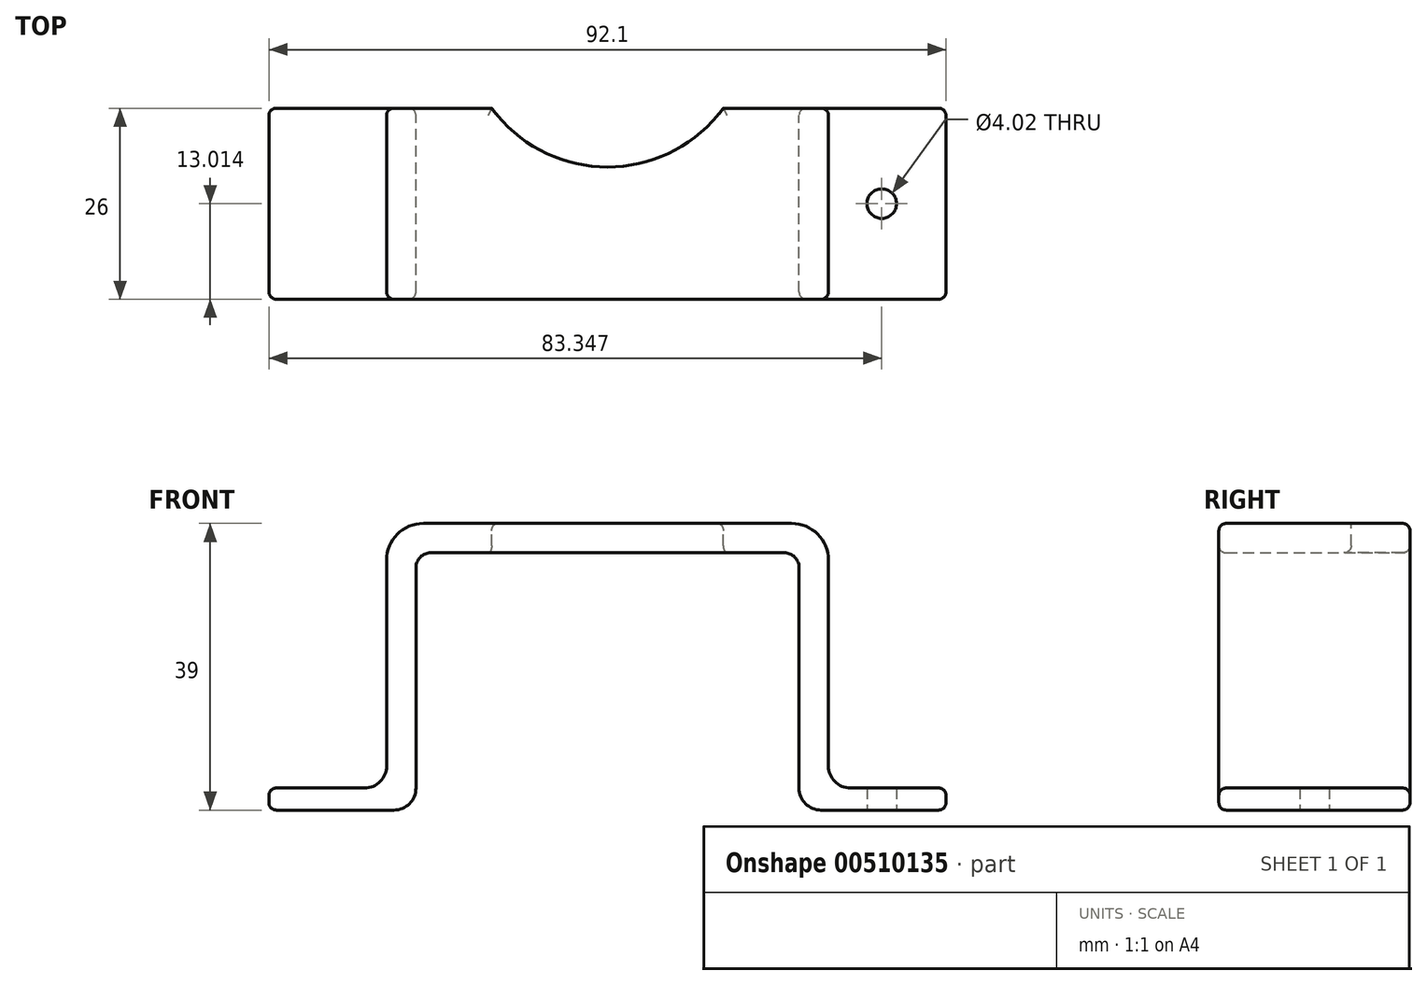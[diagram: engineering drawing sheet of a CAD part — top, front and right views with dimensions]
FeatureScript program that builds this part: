
annotation { "Feature Type Name" : "Feature", "Feature Type Description" : "" }
export const myFeature = defineFeature(function(context is Context, id is Id, definition is map)
    precondition{}
    {
        {
            var Q0;
            Q0=qCreatedBy(makeId("Front.planeOp"),FACE);
            var sketch = newSketch(context, id + "F0", { "sketchPlane" : qUnion([Q0])});
            skLineSegment(sketch, "E0.bottom", {"start": v(-24.05, 17.5) * mm, "end": v(24.05, 17.5) * mm});
            skLineSegment(sketch, "E0.left", {"start": v(-26.05, 15.5) * mm, "end": v(-26.05, -14.5) * mm});
            skLineSegment(sketch, "E0.right", {"start": v(26.05, 15.5) * mm, "end": v(26.05, -14.5) * mm});
            skPoint(sketch, "E0.middle", {"position": v(0, 0) * mm});
            skLineSegment(sketch, "E1.0", {"start": v(-30.05, 17.5) * mm, "end": v(-30.05, -11.5) * mm});
            skLineSegment(sketch, "E2.0", {"start": v(-26.05, 21.5) * mm, "end": v(26.05, 21.5) * mm});
            skLineSegment(sketch, "E3.bottom", {"start": v(-25.05, 21.5) * mm, "end": v(-26.05, 21.5) * mm});
            skLineSegment(sketch, "E3.right", {"start": v(-30.05, 17.5) * mm, "end": v(-30.05, 16.5) * mm});
            skLineSegment(sketch, "E4.bottom", {"start": v(-30.05, -17.5) * mm, "end": v(-45.05, -17.5) * mm});
            skLineSegment(sketch, "E4.top", {"start": v(-33.05, -14.5) * mm, "end": v(-45.05, -14.5) * mm});
            skLineSegment(sketch, "E4.right", {"start": v(-46.05, -16.5) * mm, "end": v(-46.05, -15.5) * mm});
            skLineSegment(sketch, "E5", {"start": v(-30.05, -17.5) * mm, "end": v(-29.05, -17.5) * mm});
            skLineSegment(sketch, "E6.MirrorCS", {"start": v(30.05, 17.5) * mm, "end": v(30.05, 16.5) * mm});
            skLineSegment(sketch, "E7.MirrorCS", {"start": v(25.05, 21.5) * mm, "end": v(26.05, 21.5) * mm});
            skLineSegment(sketch, "E8.MirrorCS", {"start": v(30.05, 17.5) * mm, "end": v(30.05, -11.5) * mm});
            skLineSegment(sketch, "E9.MirrorCS", {"start": v(33.05, -14.5) * mm, "end": v(45.05, -14.5) * mm});
            skLineSegment(sketch, "E10.MirrorCS", {"start": v(46.05, -16.5) * mm, "end": v(46.05, -15.5) * mm});
            skLineSegment(sketch, "E11.MirrorCS", {"start": v(30.05, -17.5) * mm, "end": v(45.05, -17.5) * mm});
            skLineSegment(sketch, "E12.MirrorCS", {"start": v(30.05, -17.5) * mm, "end": v(29.05, -17.5) * mm});
            skPoint(sketch, "E13.orphan", {"position": v(30.05, -17.5) * mm});
            skPoint(sketch, "E14.visualSharp", {"position": v(-30.05, 21.5) * mm});
            skArc(sketch, "E14.filletArc", {"start": v(-25.05, 21.5) * mm, "mid": v(-28.59, 20.04) * mm, "end": v(-30.05, 16.5) * mm});
            skPoint(sketch, "E15.visualSharp", {"position": v(-30.05, -14.5) * mm});
            skArc(sketch, "E15.filletArc", {"start": v(-33.05, -14.5) * mm, "mid": v(-30.93, -13.62) * mm, "end": v(-30.05, -11.5) * mm});
            skPoint(sketch, "E16.visualSharp", {"position": v(-46.05, -14.5) * mm});
            skArc(sketch, "E16.filletArc", {"start": v(-45.05, -14.5) * mm, "mid": v(-45.76, -14.8) * mm, "end": v(-46.05, -15.5) * mm});
            skPoint(sketch, "E17.visualSharp", {"position": v(-46.05, -17.5) * mm});
            skArc(sketch, "E17.filletArc", {"start": v(-46.05, -16.5) * mm, "mid": v(-45.76, -17.2) * mm, "end": v(-45.05, -17.5) * mm});
            skPoint(sketch, "E18.visualSharp", {"position": v(-26.05, -17.5) * mm});
            skArc(sketch, "E18.filletArc", {"start": v(-29.05, -17.5) * mm, "mid": v(-26.93, -16.62) * mm, "end": v(-26.05, -14.5) * mm});
            skPoint(sketch, "E19.visualSharp", {"position": v(-26.05, 17.5) * mm});
            skArc(sketch, "E19.filletArc", {"start": v(-24.05, 17.5) * mm, "mid": v(-25.46, 16.91) * mm, "end": v(-26.05, 15.5) * mm});
            skPoint(sketch, "E20.visualSharp", {"position": v(26.05, 17.5) * mm});
            skArc(sketch, "E20.filletArc", {"start": v(26.05, 15.5) * mm, "mid": v(25.46, 16.91) * mm, "end": v(24.05, 17.5) * mm});
            skArc(sketch, "E21.MirrorCS", {"start": v(25.05, 21.5) * mm, "mid": v(28.59, 20.04) * mm, "end": v(30.05, 16.5) * mm});
            skArc(sketch, "E22.MirrorCS", {"start": v(33.05, -14.5) * mm, "mid": v(30.93, -13.62) * mm, "end": v(30.05, -11.5) * mm});
            skArc(sketch, "E23.MirrorCS", {"start": v(29.05, -17.5) * mm, "mid": v(26.93, -16.62) * mm, "end": v(26.05, -14.5) * mm});
            skArc(sketch, "E24.MirrorCS", {"start": v(45.05, -14.5) * mm, "mid": v(45.76, -14.8) * mm, "end": v(46.05, -15.5) * mm});
            skArc(sketch, "E25.MirrorCS", {"start": v(46.05, -16.5) * mm, "mid": v(45.76, -17.2) * mm, "end": v(45.05, -17.5) * mm});
            skPoint(sketch, "E26.orphan", {"position": v(30.05, -14.5) * mm});
            skPoint(sketch, "E27.orphan", {"position": v(26.05, -17.5) * mm});
            skPoint(sketch, "E28.orphan", {"position": v(46.05, -17.5) * mm});
            skPoint(sketch, "E29.orphan", {"position": v(46.05, -14.5) * mm});
            skSolve(sketch);
        }
        {
            var Q0;
            Q0=makeQuery(id+"F0.imprint","IMPRINT",FACE,{"disambiguationData":[TD([[makeQuery(id+"F0.imprint","IMPRINT",EDGE,{"derivedFrom":sQuery(id+"F0.wireOp",EDGE,"E0.bottom")}),1.0]])]});
            extrude(context, id + "F1", {"entities" : qUnion([Q0]), "depth" : 26 * mm, "symmetric" : true});
        }
        {
            var Q0;
            Q0=makeQuery(id+"F1.opExtrude","SWEPT_FACE",FACE,{"disambiguationData":[OSD([sQuery(id+"F0.wireOp",EDGE,"E2.0")])]});
            var sketch = newSketch(context, id + "F2", { "sketchPlane" : qUnion([Q0])});
            skCircle(sketch, "E30", {"center": v(0, 24.5) * mm, "radius": 19.5 * mm});
            skCircle(sketch, "E31.MirrorC", {"center": v(0, -24.5) * mm, "radius": 19.5 * mm});
            skSolve(sketch);
        }
        {
            var Q0;
            {var subQ0=sQuery(id+"F2.wireOp",EDGE,"E30");var subQ1=makeQuery(id+"F1.opExtrude","CAP_EDGE",EDGE,{"disambiguationData":[OSD([sQuery(id+"F0.wireOp",EDGE,"E2.0")])],"isStart":true});var subQ2=makeQuery(id+"F2.imprint","INTERSECT",VERTEX,{"disambiguationData":[OD(0.0)],"derivedFrom":[subQ1,subQ0]});Q0=makeQuery(id+"F2.imprint","IMPRINT",FACE,{"disambiguationData":[TD([[makeQuery(id+"F2.imprint","IMPRINT",EDGE,{"disambiguationData":[TD([[subQ2,-1.0]])],"derivedFrom":subQ0}),1.0]])]});}
            var Q1;
            {var subQ0=sQuery(id+"F2.wireOp",EDGE,"E31.MirrorC");var subQ1=makeQuery(id+"F1.opExtrude","CAP_EDGE",EDGE,{"disambiguationData":[OSD([sQuery(id+"F0.wireOp",EDGE,"E2.0")])],"isStart":false});var subQ2=makeQuery(id+"F2.imprint","INTERSECT",VERTEX,{"disambiguationData":[OD(0.0)],"derivedFrom":[subQ1,subQ0]});Q1=makeQuery(id+"F2.imprint","IMPRINT",FACE,{"disambiguationData":[TD([[makeQuery(id+"F2.imprint","IMPRINT",EDGE,{"disambiguationData":[TD([[subQ2,-1.0]])],"derivedFrom":subQ0}),-1.0]])]});}
            extrude(context, id + "F3", {"entities" : qUnion([Q0, Q1]), "operationType" : NewBodyOperationType.REMOVE, "endBound" : BoundingType.THROUGH_ALL, "oppositeDirection" : true, "depth" : 25 * mm});
        }
        {
            var Q0;
            Q0=makeQuery(id+"F1.opExtrude","SWEPT_FACE",FACE,{"disambiguationData":[OSD([sQuery(id+"F0.wireOp",EDGE,"E11.MirrorCS"),sQuery(id+"F0.wireOp",EDGE,"E12.MirrorCS")])]});
            var sketch = newSketch(context, id + "F4", { "sketchPlane" : qUnion([Q0])});
            skCircle(sketch, "E32", {"center": v(37.3, -0.01) * mm, "radius": 2.01 * mm});
            skCircle(sketch, "E33.MirrorC", {"center": v(-37.3, -0.01) * mm, "radius": 2.01 * mm});
            skSolve(sketch);
        }
        {
            var Q0;
            Q0=makeQuery(id+"F4.imprint","IMPRINT",FACE,{"disambiguationData":[TD([[makeQuery(id+"F4.imprint","IMPRINT",EDGE,{"derivedFrom":sQuery(id+"F4.wireOp",EDGE,"E32")}),1.0]])]});
            var Q1;
            Q1=makeQuery(id+"F4.imprint","IMPRINT",FACE,{"disambiguationData":[TD([[makeQuery(id+"F4.imprint","IMPRINT",EDGE,{"derivedFrom":sQuery(id+"F4.wireOp",EDGE,"E33.MirrorC")}),-1.0]])]});
            var Q2;
            Q2=sQuery(id+"F4.wireOp",EDGE,"E32");
            var Q3;
            Q3=sQuery(id+"F4.wireOp",EDGE,"E33.MirrorC");
            extrude(context, id + "F5", {"entities" : qUnion([Q0, Q1]), "operationType" : NewBodyOperationType.REMOVE, "surfaceEntities" : qUnion([Q2, Q3]), "endBound" : BoundingType.THROUGH_ALL, "oppositeDirection" : true, "depth" : 25 * mm});
        }
        {
            var Q0;
            Q0=makeQuery(id+"F1.opExtrude","CAP_EDGE",EDGE,{"disambiguationData":[OSD([sQuery(id+"F0.wireOp",EDGE,"E1.0")])],"isStart":false});
            var Q1;
            Q1=makeQuery(id+"F1.opExtrude","CAP_EDGE",EDGE,{"disambiguationData":[OSD([sQuery(id+"F0.wireOp",EDGE,"E14.filletArc")])],"isStart":false});
            var Q2;
            {var subQ0=sQuery(id+"F0.wireOp",EDGE,"E14.filletArc");var subQ1=sQuery(id+"F0.wireOp",EDGE,"E2.0");Q2=makeQuery(id+"F3.boolean.opBoolean","SPLIT",EDGE,{"disambiguationData":[TD([makeQuery(id+"F1.opExtrude","SWEPT_FACE",FACE,{"disambiguationData":[OSD([subQ0])]})])],"derivedFrom":makeQuery(id+"F1.opExtrude","CAP_EDGE",EDGE,{"disambiguationData":[OSD([subQ1])],"isStart":false})});}
            var Q3;
            Q3=makeQuery(id+"F3.boolean.opBoolean","COPY",EDGE,{"derivedFrom":makeQuery(id+"F3.opExtrude","CAP_EDGE",EDGE,{"disambiguationData":[OSD([sQuery(id+"F2.wireOp",EDGE,"E31.MirrorC")])],"isStart":true})});
            var Q4;
            Q4=makeQuery(id+"F3.boolean.opBoolean","INTERSECT",EDGE,{"derivedFrom":[makeQuery(id+"F1.opExtrude","SWEPT_FACE",FACE,{"disambiguationData":[OSD([sQuery(id+"F0.wireOp",EDGE,"E0.bottom")])]}),makeQuery(id+"F3.opExtrude","SWEPT_FACE",FACE,{"disambiguationData":[OSD([sQuery(id+"F2.wireOp",EDGE,"E31.MirrorC")])]})]});
            var Q5;
            {var subQ0=sQuery(id+"F0.wireOp",EDGE,"E0.bottom");var subQ1=sQuery(id+"F0.wireOp",EDGE,"E20.filletArc");Q5=makeQuery(id+"F3.boolean.opBoolean","SPLIT",EDGE,{"disambiguationData":[TD([makeQuery(id+"F1.opExtrude","SWEPT_FACE",FACE,{"disambiguationData":[OSD([subQ1])]})])],"derivedFrom":makeQuery(id+"F1.opExtrude","CAP_EDGE",EDGE,{"disambiguationData":[OSD([subQ0])],"isStart":false})});}
            var Q6;
            {var subQ0=sQuery(id+"F0.wireOp",EDGE,"E21.MirrorCS");var subQ1=sQuery(id+"F0.wireOp",EDGE,"E2.0");Q6=makeQuery(id+"F3.boolean.opBoolean","SPLIT",EDGE,{"disambiguationData":[TD([makeQuery(id+"F1.opExtrude","SWEPT_FACE",FACE,{"disambiguationData":[OSD([subQ0])]})])],"derivedFrom":makeQuery(id+"F1.opExtrude","CAP_EDGE",EDGE,{"disambiguationData":[OSD([subQ1])],"isStart":false})});}
            var Q7;
            Q7=makeQuery(id+"F1.opExtrude","CAP_EDGE",EDGE,{"disambiguationData":[OSD([sQuery(id+"F0.wireOp",EDGE,"E21.MirrorCS")])],"isStart":false});
            var Q8;
            Q8=makeQuery(id+"F1.opExtrude","SWEPT_EDGE",EDGE,{"disambiguationData":[OSD([sQuery(id+"F0.wireOp",EDGE,"E0.bottom"),sQuery(id+"F0.wireOp",EDGE,"E20.filletArc")])]});
            var Q9;
            Q9=makeQuery(id+"F1.opExtrude","CAP_EDGE",EDGE,{"disambiguationData":[OSD([sQuery(id+"F0.wireOp",EDGE,"E8.MirrorCS")])],"isStart":true});
            var Q10;
            Q10=makeQuery(id+"F3.boolean.opBoolean","COPY",EDGE,{"derivedFrom":makeQuery(id+"F3.opExtrude","CAP_EDGE",EDGE,{"disambiguationData":[OSD([sQuery(id+"F2.wireOp",EDGE,"E30")])],"isStart":true})});
            var Q11;
            Q11=makeQuery(id+"F3.boolean.opBoolean","INTERSECT",EDGE,{"derivedFrom":[makeQuery(id+"F1.opExtrude","SWEPT_FACE",FACE,{"disambiguationData":[OSD([sQuery(id+"F0.wireOp",EDGE,"E0.bottom")])]}),makeQuery(id+"F3.opExtrude","SWEPT_FACE",FACE,{"disambiguationData":[OSD([sQuery(id+"F2.wireOp",EDGE,"E30")])]})]});
            var Q12;
            Q12=makeQuery(id+"F1.opExtrude","CAP_EDGE",EDGE,{"disambiguationData":[OSD([sQuery(id+"F0.wireOp",EDGE,"E19.filletArc")])],"isStart":true});
            fillet(context, id + "F6", {"entities" : qUnion([Q0, Q1, Q2, Q3, Q4, Q5, Q6, Q7, Q8, Q9, Q10, Q11, Q12]), "radius" : 1 * mm, "tangentPropagation" : true, "allowEdgeOverflow" : false});
        }
    });
